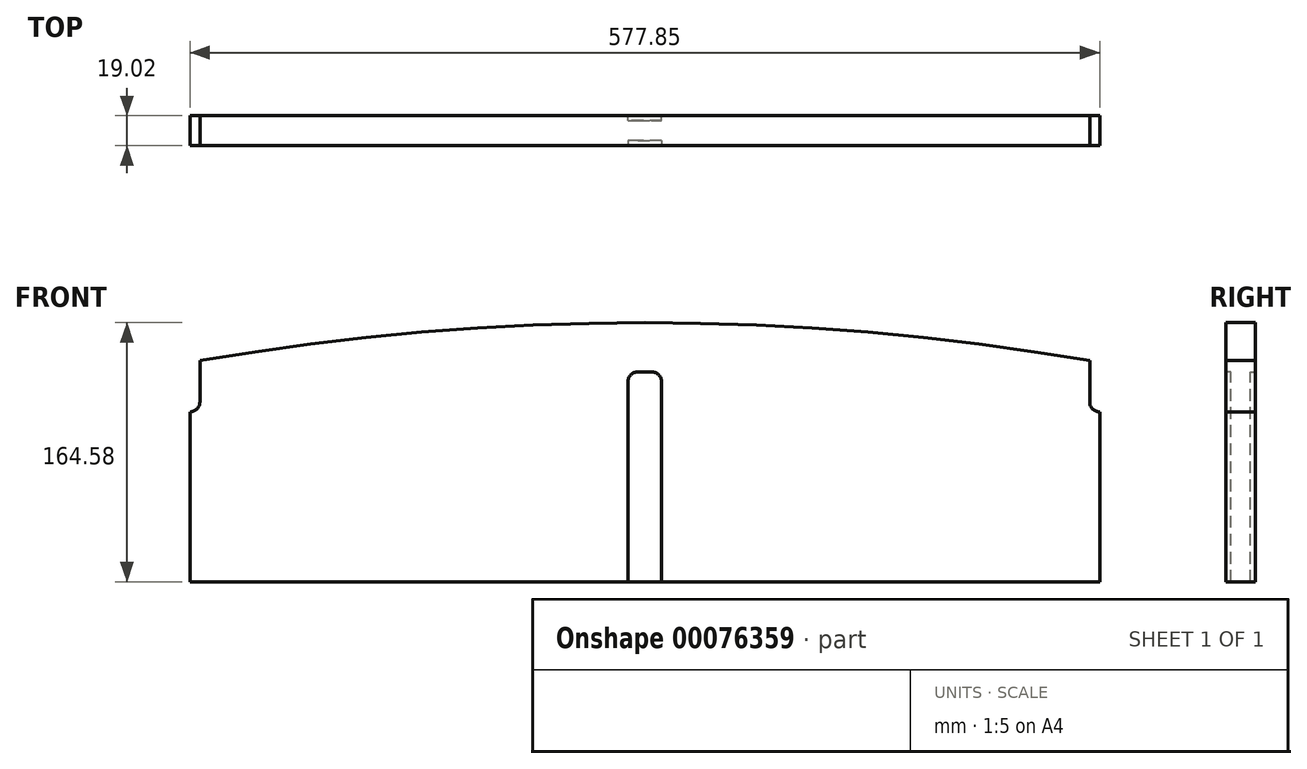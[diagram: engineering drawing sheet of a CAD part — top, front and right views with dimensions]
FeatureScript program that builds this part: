
annotation { "Feature Type Name" : "Feature", "Feature Type Description" : "" }
export const myFeature = defineFeature(function(context is Context, id is Id, definition is map)
    precondition{}
    {
        {
            var Q0;
            Q0=qCreatedBy(makeId("Front.planeOp"),FACE);
            var sketch = newSketch(context, id + "F0", { "sketchPlane" : qUnion([Q0])});
            skLineSegment(sketch, "E0.rect.bottom", {"start": v(285.75, -70.25) * mm, "end": v(-292.1, -70.25) * mm});
            skLineSegment(sketch, "E0.rect.left", {"start": v(285.75, -70.25) * mm, "end": v(285.75, 37.7) * mm});
            skLineSegment(sketch, "E0.rect.right", {"start": v(-292.1, -70.25) * mm, "end": v(-292.1, 37.7) * mm});
            skPoint(sketch, "E0.rect.middle", {"position": v(0, 0) * mm});
            skArc(sketch, "E1", {"start": v(279.4, 70.25) * mm, "mid": v(-3.18, 94.33) * mm, "end": v(-285.75, 70.25) * mm});
            skLineSegment(sketch, "E2.bottom", {"start": v(285.75, 37.7) * mm, "end": v(285.75, 37.7) * mm});
            skLineSegment(sketch, "E2.right", {"start": v(279.4, 44.05) * mm, "end": v(279.4, 70.25) * mm});
            skPoint(sketch, "E3.visualSharp", {"position": v(279.4, 37.7) * mm});
            skArc(sketch, "E3.filletArc", {"start": v(279.4, 44.05) * mm, "mid": v(281.26, 39.56) * mm, "end": v(285.75, 37.7) * mm});
            skLineSegment(sketch, "E4", {"start": v(-3.17, -70.25) * mm, "end": v(-3.17, 119.27) * mm, "construction": true});
            skPoint(sketch, "E4.endSnap0", {"position": v(-3.17, -70.25) * mm});
            skArc(sketch, "E5.MirrorCS", {"start": v(-285.75, 44.05) * mm, "mid": v(-287.61, 39.56) * mm, "end": v(-292.1, 37.7) * mm});
            skLineSegment(sketch, "E6.MirrorCS", {"start": v(-285.75, 44.05) * mm, "end": v(-285.75, 70.25) * mm});
            skSolve(sketch);
        }
        {
            var Q0;
            Q0=makeQuery(id+"F0.imprint","IMPRINT",FACE,{"disambiguationData":[TD([[makeQuery(id+"F0.imprint","IMPRINT",EDGE,{"derivedFrom":sQuery(id+"F0.wireOp",EDGE,"E0.rect.bottom")}),-1.0]])]});
            extrude(context, id + "F1", {"entities" : qUnion([Q0]), "endBound" : BoundingType.SYMMETRIC, "depth" : 19.02 * mm});
        }
        {
            var Q0;
            Q0=makeQuery(id+"F1.opExtrude","CAP_FACE",FACE,{"disambiguationData":[OSD([sQuery(id+"F0.wireOp",EDGE,"E0.rect.bottom"),sQuery(id+"F0.wireOp",EDGE,"E0.rect.left"),sQuery(id+"F0.wireOp",EDGE,"E0.rect.right"),sQuery(id+"F0.wireOp",EDGE,"E1"),sQuery(id+"F0.wireOp",EDGE,"E2.right"),sQuery(id+"F0.wireOp",EDGE,"E3.filletArc"),sQuery(id+"F0.wireOp",EDGE,"E5.MirrorCS"),sQuery(id+"F0.wireOp",EDGE,"E6.MirrorCS")])],"isStart":false});
            var sketch = newSketch(context, id + "F2", { "sketchPlane" : qUnion([Q0])});
            skLineSegment(sketch, "E7.bottom", {"start": v(-13.9, -70.25) * mm, "end": v(7.54, -70.25) * mm, "construction": true});
            skLineSegment(sketch, "E7.top", {"start": v(-7.54, 63.1) * mm, "end": v(1.2, 63.1) * mm});
            skLineSegment(sketch, "E7.left", {"start": v(-13.9, -70.25) * mm, "end": v(-13.9, 56.75) * mm});
            skLineSegment(sketch, "E7.right", {"start": v(7.54, -70.25) * mm, "end": v(7.54, 56.75) * mm});
            skPoint(sketch, "E8.visualSharp", {"position": v(-13.9, 63.1) * mm});
            skArc(sketch, "E8.filletArc", {"start": v(-7.54, 63.1) * mm, "mid": v(-12.03, 61.24) * mm, "end": v(-13.9, 56.75) * mm});
            skPoint(sketch, "E9.visualSharp", {"position": v(7.54, 63.1) * mm});
            skArc(sketch, "E9.filletArc", {"start": v(7.54, 56.75) * mm, "mid": v(5.68, 61.24) * mm, "end": v(1.2, 63.1) * mm});
            skSolve(sketch);
        }
        {
            var Q0;
            Q0=qSketchRegion(id+"F2",true);
            var Q1;
            Q1=makeQuery(id+"F2.imprint","IMPRINT",FACE,{"disambiguationData":[TD([[makeQuery(id+"F2.imprint","IMPRINT",EDGE,{"derivedFrom":sQuery(id+"F2.wireOp",EDGE,"E7.top")}),-1.0]])]});
            extrude(context, id + "F3", {"entities" : qUnion([Q0, Q1]), "operationType" : NewBodyOperationType.REMOVE, "oppositeDirection" : true, "depth" : 3.17 * mm});
        }
        {
            var Q0;
            Q0=makeQuery(id+"F1.opExtrude","CAP_FACE",FACE,{"disambiguationData":[OSD([sQuery(id+"F0.wireOp",EDGE,"E0.rect.bottom"),sQuery(id+"F0.wireOp",EDGE,"E0.rect.left"),sQuery(id+"F0.wireOp",EDGE,"E0.rect.right"),sQuery(id+"F0.wireOp",EDGE,"E1"),sQuery(id+"F0.wireOp",EDGE,"E2.right"),sQuery(id+"F0.wireOp",EDGE,"E3.filletArc"),sQuery(id+"F0.wireOp",EDGE,"E5.MirrorCS"),sQuery(id+"F0.wireOp",EDGE,"E6.MirrorCS")])],"isStart":true});
            var sketch = newSketch(context, id + "F4", { "sketchPlane" : qUnion([Q0])});
            skLineSegment(sketch, "E10.0", {"start": v(-7.54, -70.25) * mm, "end": v(-7.54, 56.75) * mm});
            skArc(sketch, "E11.0", {"start": v(-7.54, 56.75) * mm, "mid": v(-5.68, 61.24) * mm, "end": v(-1.2, 63.1) * mm});
            skLineSegment(sketch, "E12.0", {"start": v(7.54, 63.1) * mm, "end": v(-1.2, 63.1) * mm});
            skArc(sketch, "E13.0", {"start": v(7.54, 63.1) * mm, "mid": v(12.03, 61.24) * mm, "end": v(13.9, 56.75) * mm});
            skLineSegment(sketch, "E14.0", {"start": v(13.9, -70.25) * mm, "end": v(13.9, 56.75) * mm});
            skLineSegment(sketch, "E15.0", {"start": v(-7.54, -70.25) * mm, "end": v(13.9, -70.25) * mm});
            skSolve(sketch);
        }
        {
            var Q0;
            Q0=makeQuery(id+"F4.imprint","IMPRINT",FACE,{"disambiguationData":[TD([[makeQuery(id+"F4.imprint","IMPRINT",EDGE,{"derivedFrom":sQuery(id+"F4.wireOp",EDGE,"E10.0")}),-1.0]])]});
            extrude(context, id + "F5", {"entities" : qUnion([Q0]), "operationType" : NewBodyOperationType.REMOVE, "oppositeDirection" : true, "depth" : 3.17 * mm});
        }
    });
